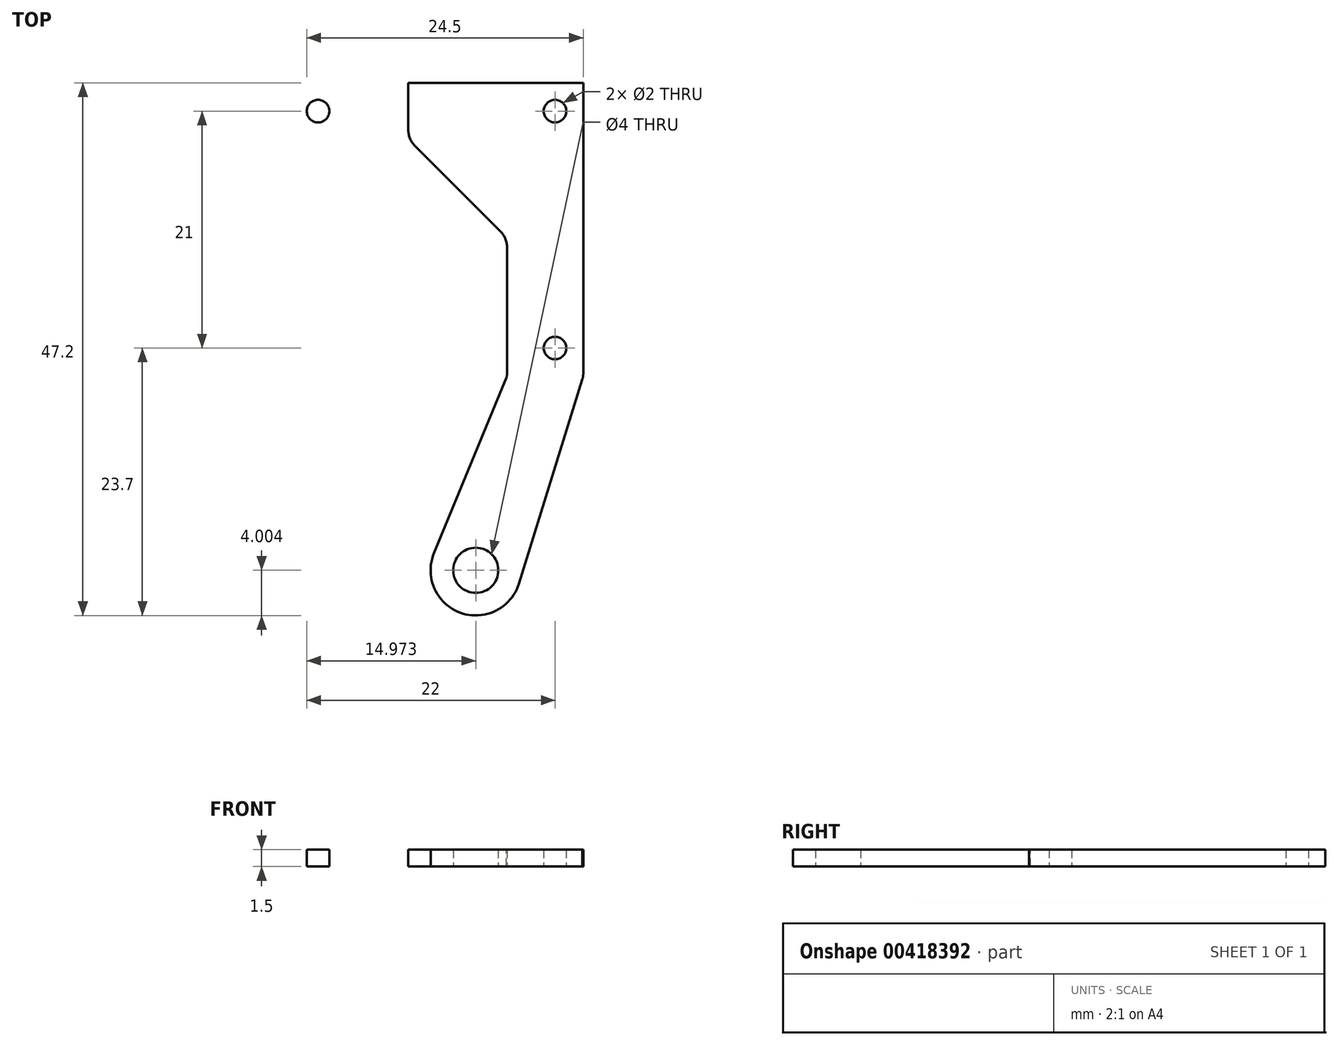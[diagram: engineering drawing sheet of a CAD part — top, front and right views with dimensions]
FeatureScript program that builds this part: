
annotation { "Feature Type Name" : "Feature", "Feature Type Description" : "" }
export const myFeature = defineFeature(function(context is Context, id is Id, definition is map)
    precondition{}
    {
        {
            var Q0;
            Q0=qCreatedBy(makeId("Top.planeOp"),FACE);
            var sketch = newSketch(context, id + "F0", { "sketchPlane" : qUnion([Q0])});
            skLineSegment(sketch, "E0.bottom", {"start": v(0, 0) * mm, "end": v(15.5, 0) * mm});
            skLineSegment(sketch, "E0.top", {"start": v(0, 26) * mm, "end": v(15.5, 26) * mm});
            skLineSegment(sketch, "E0.left", {"start": v(0, 0) * mm, "end": v(0, 26) * mm});
            skLineSegment(sketch, "E0.right", {"start": v(15.5, 0) * mm, "end": v(15.5, 26) * mm});
            skCircle(sketch, "E1", {"center": v(13, 2.5) * mm, "radius": 1 * mm});
            skArc(sketch, "E2", {"start": v(0, 8.23) * mm, "mid": v(-1.92, -1.92) * mm, "end": v(8.23, 0) * mm, "construction": true});
            skCircle(sketch, "E3", {"center": v(13, 23.5) * mm, "radius": 1 * mm});
            skLineSegment(sketch, "E4", {"start": v(2.5, 8.75) * mm, "end": v(0, 8.75) * mm});
            skLineSegment(sketch, "E5", {"start": v(8.75, 2.5) * mm, "end": v(8.75, 0) * mm});
            skArc(sketch, "E6.trimOffspring", {"start": v(8.75, 2.5) * mm, "mid": v(6.92, 6.92) * mm, "end": v(2.5, 8.75) * mm});
            skCircle(sketch, "E7", {"center": v(5.97, -17.2) * mm, "radius": 2 * mm});
            skLineSegment(sketch, "E8", {"start": v(2.5, 2.5) * mm, "end": v(5.97, -17.2) * mm, "construction": true});
            skLineSegment(sketch, "E9", {"start": v(3.13, -21.25) * mm, "end": v(10.03, -20.04) * mm});
            skPoint(sketch, "E10", {"position": v(6.58, -20.64) * mm});
            skLineSegment(sketch, "E11", {"start": v(5.97, -17.2) * mm, "end": v(6.58, -20.64) * mm, "construction": true});
            skLineSegment(sketch, "E12", {"start": v(3.13, -21.25) * mm, "end": v(2.53, -17.8) * mm});
            skLineSegment(sketch, "E13", {"start": v(2.53, -17.8) * mm, "end": v(8.75, 0) * mm});
            skLineSegment(sketch, "E14", {"start": v(10.03, -20.04) * mm, "end": v(15.5, 0) * mm});
            skLineSegment(sketch, "E15.MirrorCS", {"start": v(0, 26) * mm, "end": v(-10.5, 26) * mm});
            skCircle(sketch, "E16.MirrorC", {"center": v(-8, 23.5) * mm, "radius": 1 * mm});
            skLineSegment(sketch, "E17", {"start": v(-10.5, 21) * mm, "end": v(0, 21) * mm});
            skLineSegment(sketch, "E18", {"start": v(0, 21) * mm, "end": v(8.75, 21) * mm});
            skLineSegment(sketch, "E19", {"start": v(8.75, 21) * mm, "end": v(8.75, 2.5) * mm});
            skLineSegment(sketch, "E20", {"start": v(0, 21) * mm, "end": v(8.75, 12.25) * mm});
            skLineSegment(sketch, "E21", {"start": v(-10.5, 26) * mm, "end": v(-10.5, 21) * mm});
            skLineSegment(sketch, "E22.bottom", {"start": v(-10.5, 26) * mm, "end": v(15.5, 26) * mm});
            skLineSegment(sketch, "E22.top", {"start": v(-10.5, 31) * mm, "end": v(15.5, 31) * mm});
            skLineSegment(sketch, "E22.left", {"start": v(-10.5, 26) * mm, "end": v(-10.5, 31) * mm});
            skLineSegment(sketch, "E22.right", {"start": v(15.5, 26) * mm, "end": v(15.5, 31) * mm});
            skCircle(sketch, "E23.MirrorC", {"center": v(-8, 28.5) * mm, "radius": 1 * mm});
            skCircle(sketch, "E24.MirrorC", {"center": v(13, 28.5) * mm, "radius": 1 * mm});
            skCircle(sketch, "E25.MirrorC", {"center": v(18, 23.5) * mm, "radius": 1 * mm});
            skCircle(sketch, "E26.MirrorC", {"center": v(18, 2.5) * mm, "radius": 1 * mm});
            skLineSegment(sketch, "E27", {"start": v(15.5, 26) * mm, "end": v(20.5, 26) * mm});
            skLineSegment(sketch, "E28", {"start": v(20.5, 26) * mm, "end": v(20.5, 0) * mm});
            skLineSegment(sketch, "E29", {"start": v(20.5, 0) * mm, "end": v(15.5, 0) * mm});
            skLineSegment(sketch, "E30.MirrorCS", {"start": v(41.5, 26) * mm, "end": v(15.5, 26) * mm});
            skLineSegment(sketch, "E31.MirrorCS", {"start": v(41.5, 26) * mm, "end": v(41.5, 21) * mm});
            skLineSegment(sketch, "E32.MirrorCS", {"start": v(41.5, 21) * mm, "end": v(31, 21) * mm});
            skLineSegment(sketch, "E33.MirrorCS", {"start": v(31, 21) * mm, "end": v(22.25, 12.25) * mm});
            skCircle(sketch, "E34.MirrorC", {"center": v(39, 23.5) * mm, "radius": 1 * mm});
            skLineSegment(sketch, "E35", {"start": v(22.25, 12.25) * mm, "end": v(20.5, 12.25) * mm});
            skLineSegment(sketch, "E36.top", {"start": v(22.25, 0) * mm, "end": v(20.5, 0) * mm});
            skLineSegment(sketch, "E36.left", {"start": v(22.25, 12.25) * mm, "end": v(22.25, 0) * mm});
            skLineSegment(sketch, "E36.right", {"start": v(20.5, 12.25) * mm, "end": v(20.5, 0) * mm});
            skSolve(sketch);
        }
        {
            var Q0;
            Q0=makeQuery(id+"F0.imprint","IMPRINT",FACE,{"disambiguationData":[TD([[makeQuery(id+"F0.imprint","IMPRINT",EDGE,{"derivedFrom":sQuery(id+"F0.wireOp",EDGE,"E16.MirrorC")}),1.0]])]});
            var Q1;
            {var subQ0=sQuery(id+"F0.wireOp",EDGE,"E18");Q1=makeQuery(id+"F0.imprint","IMPRINT",FACE,{"disambiguationData":[TD([[makeQuery(id+"F0.imprint","IMPRINT",EDGE,{"derivedFrom":subQ0}),-1.0]])]});}
            var Q2;
            {var subQ0=sQuery(id+"F0.wireOp",EDGE,"E0.right");Q2=makeQuery(id+"F0.imprint","IMPRINT",FACE,{"disambiguationData":[TD([[makeQuery(id+"F0.imprint","IMPRINT",EDGE,{"derivedFrom":subQ0}),1.0]])]});}
            var Q3;
            Q3=makeQuery(id+"F0.imprint","IMPRINT",FACE,{"disambiguationData":[TD([[makeQuery(id+"F0.imprint","IMPRINT",EDGE,{"derivedFrom":sQuery(id+"F0.wireOp",EDGE,"E7")}),-1.0]])]});
            extrude(context, id + "F1", {"entities" : qUnion([Q0, Q1, Q2, Q3]), "depth" : 1.5 * mm});
        }
        {
            var Q0;
            Q0=makeQuery(id+"F1.opExtrude","SWEPT_EDGE",EDGE,{"disambiguationData":[OSD([sQuery(id+"F0.wireOp",EDGE,"E9"),sQuery(id+"F0.wireOp",EDGE,"E12")])]});
            var Q1;
            Q1=makeQuery(id+"F1.opExtrude","SWEPT_EDGE",EDGE,{"disambiguationData":[OSD([sQuery(id+"F0.wireOp",EDGE,"E12"),sQuery(id+"F0.wireOp",EDGE,"E13")])]});
            var Q2;
            Q2=makeQuery(id+"F1.opExtrude","SWEPT_EDGE",EDGE,{"disambiguationData":[OSD([sQuery(id+"F0.wireOp",EDGE,"E9"),sQuery(id+"F0.wireOp",EDGE,"E14")])]});
            var Q3;
            Q3=makeQuery(id+"F1.opExtrude","SWEPT_EDGE",EDGE,{"disambiguationData":[OSD([sQuery(id+"F0.wireOp",EDGE,"E0.left"),sQuery(id+"F0.wireOp",EDGE,"E17"),sQuery(id+"F0.wireOp",EDGE,"E18"),sQuery(id+"F0.wireOp",EDGE,"E20")])]});
            var Q4;
            Q4=makeQuery(id+"F1.opExtrude","SWEPT_EDGE",EDGE,{"disambiguationData":[OSD([sQuery(id+"F0.wireOp",EDGE,"E19"),sQuery(id+"F0.wireOp",EDGE,"E20")])]});
            var Q5;
            Q5=makeQuery(id+"F1.opExtrude","SWEPT_EDGE",EDGE,{"disambiguationData":[OSD([sQuery(id+"F0.wireOp",EDGE,"E0.bottom"),sQuery(id+"F0.wireOp",EDGE,"E5"),sQuery(id+"F0.wireOp",EDGE,"E13")])]});
            var Q6;
            Q6=makeQuery(id+"F1.opExtrude","SWEPT_EDGE",EDGE,{"disambiguationData":[OSD([sQuery(id+"F0.wireOp",EDGE,"E0.bottom"),sQuery(id+"F0.wireOp",EDGE,"E0.right"),sQuery(id+"F0.wireOp",EDGE,"E14"),sQuery(id+"F0.wireOp",EDGE,"E29")])]});
            var Q7;
            Q7=makeQuery(id+"F1.opExtrude","SWEPT_EDGE",EDGE,{"disambiguationData":[OSD([sQuery(id+"F0.wireOp",EDGE,"E17"),sQuery(id+"F0.wireOp",EDGE,"E21")])]});
            var Q8;
            Q8=makeQuery(id+"F1.opExtrude","SWEPT_EDGE",EDGE,{"disambiguationData":[OSD([sQuery(id+"F0.wireOp",EDGE,"E21"),sQuery(id+"F0.wireOp",EDGE,"E22.bottom"),sQuery(id+"F0.wireOp",EDGE,"E22.left")])]});
            var Q9;
            Q9=makeQuery(id+"F1.opExtrude","SWEPT_EDGE",EDGE,{"disambiguationData":[OSD([sQuery(id+"F0.wireOp",EDGE,"E30.MirrorCS"),sQuery(id+"F0.wireOp",EDGE,"E31.MirrorCS")])]});
            var Q10;
            Q10=makeQuery(id+"F1.opExtrude","SWEPT_EDGE",EDGE,{"disambiguationData":[OSD([sQuery(id+"F0.wireOp",EDGE,"E31.MirrorCS"),sQuery(id+"F0.wireOp",EDGE,"E32.MirrorCS")])]});
            var Q11;
            Q11=makeQuery(id+"F1.opExtrude","SWEPT_EDGE",EDGE,{"disambiguationData":[OSD([sQuery(id+"F0.wireOp",EDGE,"E32.MirrorCS"),sQuery(id+"F0.wireOp",EDGE,"E33.MirrorCS")])]});
            var Q12;
            Q12=makeQuery(id+"F1.opExtrude","SWEPT_EDGE",EDGE,{"disambiguationData":[OSD([sQuery(id+"F0.wireOp",EDGE,"E33.MirrorCS"),sQuery(id+"F0.wireOp",EDGE,"E35"),sQuery(id+"F0.wireOp",EDGE,"E36.left")])]});
            var Q13;
            Q13=makeQuery(id+"F1.opExtrude","SWEPT_EDGE",EDGE,{"disambiguationData":[OSD([sQuery(id+"F0.wireOp",EDGE,"E36.top"),sQuery(id+"F0.wireOp",EDGE,"E36.left")])]});
            fillet(context, id + "F2", {"entities" : qUnion([Q0, Q1, Q2, Q3, Q4, Q5, Q6, Q7, Q8, Q9, Q10, Q11, Q12, Q13]), "radius" : 2 * mm, "tangentPropagation" : true, "allowEdgeOverflow" : false});
        }
        {
            var Q0;
            Q0=makeQuery(id+"F1.opExtrude","CAP_FACE",FACE,{"disambiguationData":[OSD([sQuery(id+"F0.wireOp",EDGE,"E0.right"),sQuery(id+"F0.wireOp",EDGE,"E1"),sQuery(id+"F0.wireOp",EDGE,"E3"),sQuery(id+"F0.wireOp",EDGE,"E5"),sQuery(id+"F0.wireOp",EDGE,"E7"),sQuery(id+"F0.wireOp",EDGE,"E9"),sQuery(id+"F0.wireOp",EDGE,"E12"),sQuery(id+"F0.wireOp",EDGE,"E13"),sQuery(id+"F0.wireOp",EDGE,"E14"),sQuery(id+"F0.wireOp",EDGE,"E16.MirrorC"),sQuery(id+"F0.wireOp",EDGE,"E17"),sQuery(id+"F0.wireOp",EDGE,"E19"),sQuery(id+"F0.wireOp",EDGE,"E20"),sQuery(id+"F0.wireOp",EDGE,"E21"),sQuery(id+"F0.wireOp",EDGE,"E22.top"),sQuery(id+"F0.wireOp",EDGE,"E22.left"),sQuery(id+"F0.wireOp",EDGE,"E22.right"),sQuery(id+"F0.wireOp",EDGE,"E23.MirrorC"),sQuery(id+"F0.wireOp",EDGE,"E24.MirrorC")])],"isStart":false});
            var sketch = newSketch(context, id + "F3", { "sketchPlane" : qUnion([Q0])});
            skCircle(sketch, "E37", {"center": v(5.97, -17.2) * mm, "radius": 4 * mm});
            skLineSegment(sketch, "E38", {"start": v(8.75, 0) * mm, "end": v(2.28, -15.67) * mm});
            skLineSegment(sketch, "E39", {"start": v(15.43, -0.26) * mm, "end": v(9.8, -18.38) * mm});
            skSolve(sketch);
        }
        {
            var Q0;
            {var subQ3=sQuery(id+"F3.wireOp",EDGE,"E39");Q0=makeQuery(id+"F3.imprint","IMPRINT",FACE,{"disambiguationData":[TD([[makeQuery(id+"F3.imprint","IMPRINT",EDGE,{"derivedFrom":subQ3}),1.0]])]});}
            var Q1;
            {var subQ0=sQuery(id+"F3.wireOp",EDGE,"E37");var subQ1=sQuery(id+"F0.wireOp",EDGE,"E12");var subQ2=sQuery(id+"F0.wireOp",EDGE,"E9");var subQ3=makeQuery(id+"F2.opFillet","BLEND_EDGE",EDGE,{"blendedFrom":[makeQuery(id+"F1.opExtrude","SWEPT_EDGE",EDGE,{"disambiguationData":[OSD([subQ2,subQ1])]}),makeQuery(id+"F1.opExtrude","CAP_FACE",FACE,{"disambiguationData":[OSD([sQuery(id+"F0.wireOp",EDGE,"E0.right"),sQuery(id+"F0.wireOp",EDGE,"E1"),sQuery(id+"F0.wireOp",EDGE,"E3"),sQuery(id+"F0.wireOp",EDGE,"E5"),sQuery(id+"F0.wireOp",EDGE,"E7"),subQ2,subQ1,sQuery(id+"F0.wireOp",EDGE,"E13"),sQuery(id+"F0.wireOp",EDGE,"E14"),sQuery(id+"F0.wireOp",EDGE,"E16.MirrorC"),sQuery(id+"F0.wireOp",EDGE,"E17"),sQuery(id+"F0.wireOp",EDGE,"E19"),sQuery(id+"F0.wireOp",EDGE,"E20"),sQuery(id+"F0.wireOp",EDGE,"E21"),sQuery(id+"F0.wireOp",EDGE,"E22.top"),sQuery(id+"F0.wireOp",EDGE,"E22.left"),sQuery(id+"F0.wireOp",EDGE,"E22.right"),sQuery(id+"F0.wireOp",EDGE,"E23.MirrorC"),sQuery(id+"F0.wireOp",EDGE,"E24.MirrorC")])],"isStart":false})],"blendedInto":[makeQuery(id+"F1.opExtrude","CAP_FACE",FACE,{"disambiguationData":[OSD([sQuery(id+"F0.wireOp",EDGE,"E0.right"),sQuery(id+"F0.wireOp",EDGE,"E1"),sQuery(id+"F0.wireOp",EDGE,"E3"),sQuery(id+"F0.wireOp",EDGE,"E5"),sQuery(id+"F0.wireOp",EDGE,"E7"),subQ2,subQ1,sQuery(id+"F0.wireOp",EDGE,"E13"),sQuery(id+"F0.wireOp",EDGE,"E14"),sQuery(id+"F0.wireOp",EDGE,"E16.MirrorC"),sQuery(id+"F0.wireOp",EDGE,"E17"),sQuery(id+"F0.wireOp",EDGE,"E19"),sQuery(id+"F0.wireOp",EDGE,"E20"),sQuery(id+"F0.wireOp",EDGE,"E21"),sQuery(id+"F0.wireOp",EDGE,"E22.top"),sQuery(id+"F0.wireOp",EDGE,"E22.left"),sQuery(id+"F0.wireOp",EDGE,"E22.right"),sQuery(id+"F0.wireOp",EDGE,"E23.MirrorC"),sQuery(id+"F0.wireOp",EDGE,"E24.MirrorC")])],"isStart":false})]});var subQ4=makeQuery(id+"F3.imprint","INTERSECT",VERTEX,{"disambiguationData":[OD(0.0)],"derivedFrom":[subQ3,subQ0]});Q1=makeQuery(id+"F3.imprint","IMPRINT",FACE,{"disambiguationData":[TD([[makeQuery(id+"F3.imprint","IMPRINT",EDGE,{"disambiguationData":[TD([[subQ4,-1.0]])],"derivedFrom":subQ0}),-1.0]])]});}
            var Q2;
            {var subQ0=sQuery(id+"F0.wireOp",EDGE,"E9");var subQ1=makeQuery(id+"F1.opExtrude","CAP_EDGE",EDGE,{"disambiguationData":[OSD([subQ0])],"isStart":false});var subQ4=sQuery(id+"F3.wireOp",EDGE,"E37");var subQ5=makeQuery(id+"F3.imprint","INTERSECT",VERTEX,{"derivedFrom":[subQ1,subQ4]});Q2=makeQuery(id+"F3.imprint","IMPRINT",FACE,{"disambiguationData":[TD([[makeQuery(id+"F3.imprint","IMPRINT",EDGE,{"disambiguationData":[TD([[subQ5,-1.0]])],"derivedFrom":subQ4}),-1.0]])]});}
            extrude(context, id + "F4", {"entities" : qUnion([Q0, Q1, Q2]), "operationType" : NewBodyOperationType.REMOVE, "endBound" : BoundingType.UP_TO_NEXT, "oppositeDirection" : true, "depth" : 25 * mm});
        }
        {
            var Q0;
            {var subQ0=sQuery(id+"F3.wireOp",EDGE,"E38");var subQ1=sQuery(id+"F3.wireOp",EDGE,"E37");var subQ2=makeQuery(id+"F3.imprint","INTERSECT",VERTEX,{"derivedFrom":[subQ1,subQ0]});Q0=makeQuery(id+"F3.imprint","IMPRINT",FACE,{"disambiguationData":[TD([[makeQuery(id+"F3.imprint","IMPRINT",EDGE,{"disambiguationData":[TD([[subQ2,1.0]])],"derivedFrom":subQ1}),-1.0]])]});}
            var Q1;
            {var subQ0=sQuery(id+"F0.wireOp",EDGE,"E12");var subQ1=makeQuery(id+"F1.opExtrude","CAP_EDGE",EDGE,{"disambiguationData":[OSD([subQ0])],"isStart":false});Q1=makeQuery(id+"F3.imprint","IMPRINT",FACE,{"disambiguationData":[TD([[makeQuery(id+"F3.imprint","IMPRINT",EDGE,{"derivedFrom":subQ1}),1.0]])]});}
            var Q2;
            {var subQ0=sQuery(id+"F3.wireOp",EDGE,"E37");var subQ2=sQuery(id+"F0.wireOp",EDGE,"E9");var subQ5=makeQuery(id+"F1.opExtrude","CAP_EDGE",EDGE,{"disambiguationData":[OSD([subQ2])],"isStart":false});var subQ6=makeQuery(id+"F3.imprint","INTERSECT",VERTEX,{"derivedFrom":[subQ5,subQ0]});Q2=makeQuery(id+"F3.imprint","IMPRINT",FACE,{"disambiguationData":[TD([[makeQuery(id+"F3.imprint","IMPRINT",EDGE,{"disambiguationData":[TD([[subQ6,1.0]])],"derivedFrom":subQ0}),1.0]])]});}
            var Q3;
            {var subQ1=sQuery(id+"F0.wireOp",EDGE,"E36.top");var subQ2=sQuery(id+"F0.wireOp",EDGE,"E29");var subQ3=sQuery(id+"F0.wireOp",EDGE,"E14");var subQ4=makeQuery(id+"F2.opFillet","BLEND_EDGE",EDGE,{"blendedFrom":[makeQuery(id+"F1.opExtrude","SWEPT_EDGE",EDGE,{"disambiguationData":[OSD([sQuery(id+"F0.wireOp",EDGE,"E0.bottom"),sQuery(id+"F0.wireOp",EDGE,"E0.right"),subQ3,subQ2])]}),makeQuery(id+"F1.opExtrude","CAP_FACE",FACE,{"disambiguationData":[OSD([sQuery(id+"F0.wireOp",EDGE,"E1"),sQuery(id+"F0.wireOp",EDGE,"E3"),sQuery(id+"F0.wireOp",EDGE,"E5"),sQuery(id+"F0.wireOp",EDGE,"E7"),sQuery(id+"F0.wireOp",EDGE,"E9"),sQuery(id+"F0.wireOp",EDGE,"E12"),sQuery(id+"F0.wireOp",EDGE,"E13"),subQ3,sQuery(id+"F0.wireOp",EDGE,"E16.MirrorC"),sQuery(id+"F0.wireOp",EDGE,"E17"),sQuery(id+"F0.wireOp",EDGE,"E19"),sQuery(id+"F0.wireOp",EDGE,"E20"),sQuery(id+"F0.wireOp",EDGE,"E21"),sQuery(id+"F0.wireOp",EDGE,"E22.bottom"),sQuery(id+"F0.wireOp",EDGE,"E25.MirrorC"),sQuery(id+"F0.wireOp",EDGE,"E26.MirrorC"),subQ2,sQuery(id+"F0.wireOp",EDGE,"E30.MirrorCS"),sQuery(id+"F0.wireOp",EDGE,"E31.MirrorCS"),sQuery(id+"F0.wireOp",EDGE,"E32.MirrorCS"),sQuery(id+"F0.wireOp",EDGE,"E33.MirrorCS"),sQuery(id+"F0.wireOp",EDGE,"E34.MirrorC"),subQ1,sQuery(id+"F0.wireOp",EDGE,"E36.left")])],"isStart":false})],"blendedInto":[makeQuery(id+"F1.opExtrude","CAP_FACE",FACE,{"disambiguationData":[OSD([sQuery(id+"F0.wireOp",EDGE,"E1"),sQuery(id+"F0.wireOp",EDGE,"E3"),sQuery(id+"F0.wireOp",EDGE,"E5"),sQuery(id+"F0.wireOp",EDGE,"E7"),sQuery(id+"F0.wireOp",EDGE,"E9"),sQuery(id+"F0.wireOp",EDGE,"E12"),sQuery(id+"F0.wireOp",EDGE,"E13"),subQ3,sQuery(id+"F0.wireOp",EDGE,"E16.MirrorC"),sQuery(id+"F0.wireOp",EDGE,"E17"),sQuery(id+"F0.wireOp",EDGE,"E19"),sQuery(id+"F0.wireOp",EDGE,"E20"),sQuery(id+"F0.wireOp",EDGE,"E21"),sQuery(id+"F0.wireOp",EDGE,"E22.bottom"),sQuery(id+"F0.wireOp",EDGE,"E25.MirrorC"),sQuery(id+"F0.wireOp",EDGE,"E26.MirrorC"),subQ2,sQuery(id+"F0.wireOp",EDGE,"E30.MirrorCS"),sQuery(id+"F0.wireOp",EDGE,"E31.MirrorCS"),sQuery(id+"F0.wireOp",EDGE,"E32.MirrorCS"),sQuery(id+"F0.wireOp",EDGE,"E33.MirrorCS"),sQuery(id+"F0.wireOp",EDGE,"E34.MirrorC"),subQ1,sQuery(id+"F0.wireOp",EDGE,"E36.left")])],"isStart":false})]});Q3=makeQuery(id+"F3.imprint","IMPRINT",FACE,{"disambiguationData":[TD([[makeQuery(id+"F3.imprint","IMPRINT",EDGE,{"derivedFrom":subQ4}),-1.0]])]});}
            var Q4;
            {var subQ3=sQuery(id+"F0.wireOp",EDGE,"E9");var subQ9=makeQuery(id+"F1.opExtrude","CAP_EDGE",EDGE,{"disambiguationData":[OSD([subQ3])],"isStart":false});Q4=makeQuery(id+"F3.imprint","IMPRINT",FACE,{"disambiguationData":[TD([[makeQuery(id+"F3.imprint","IMPRINT",EDGE,{"derivedFrom":subQ9}),-1.0]])]});}
            extrude(context, id + "F5", {"entities" : qUnion([Q0, Q1, Q2, Q3, Q4]), "operationType" : NewBodyOperationType.ADD, "oppositeDirection" : true, "depth" : 1.5 * mm});
        }
    });
